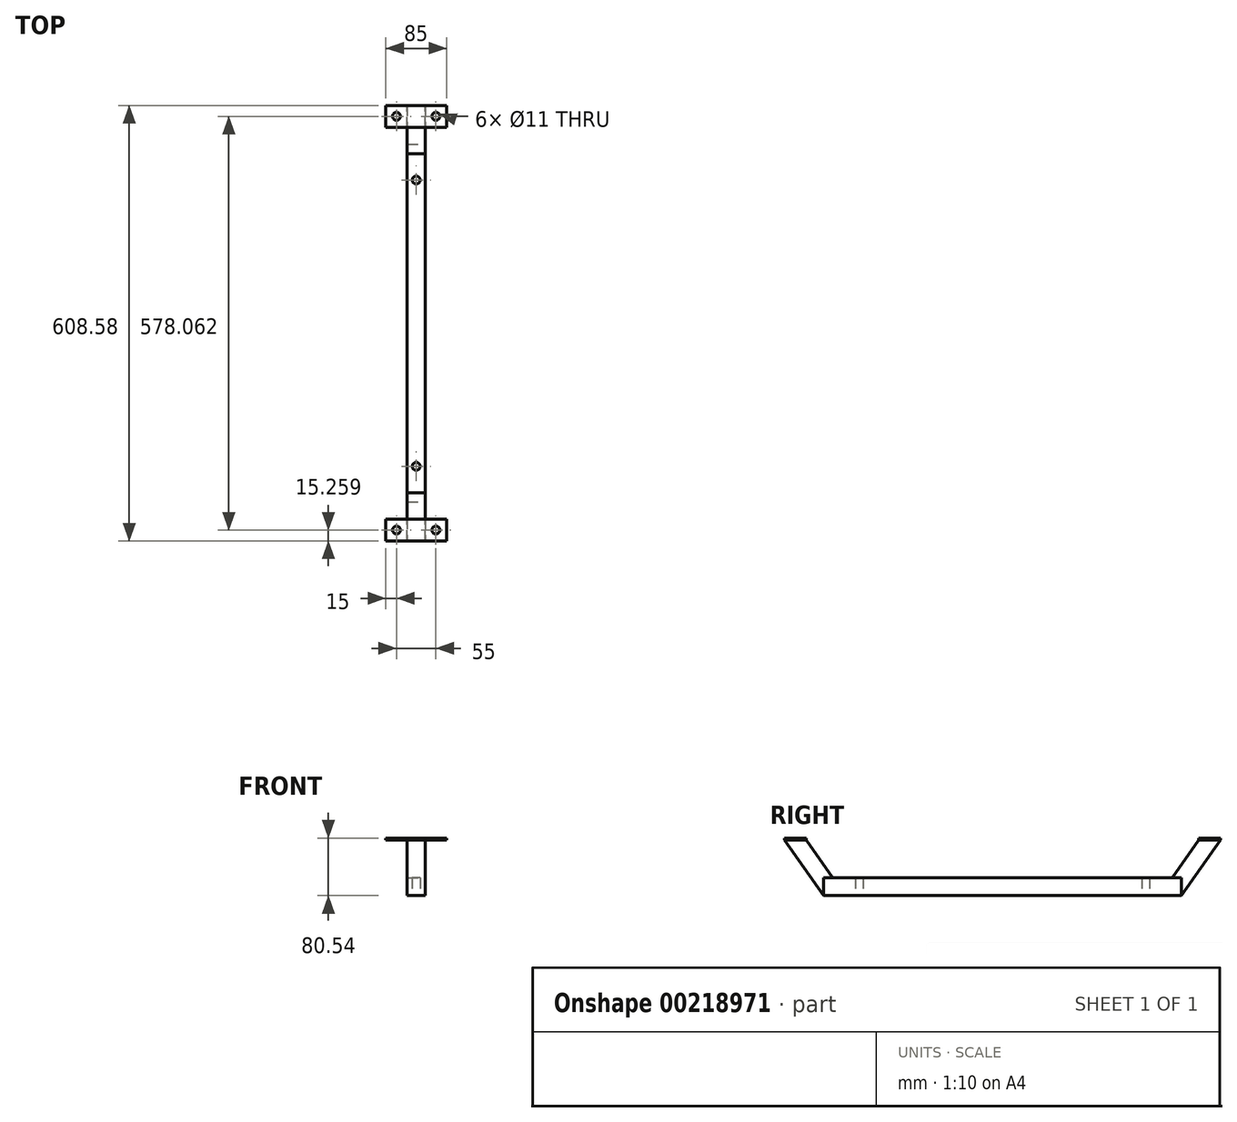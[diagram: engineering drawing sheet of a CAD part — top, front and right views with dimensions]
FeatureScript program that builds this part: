
annotation { "Feature Type Name" : "Feature", "Feature Type Description" : "" }
export const myFeature = defineFeature(function(context is Context, id is Id, definition is map)
    precondition{}
    {
        {
            var Q0;
            Q0=qCreatedBy(makeId("Top.planeOp"),FACE);
            var sketch = newSketch(context, id + "F0", { "sketchPlane" : qUnion([Q0])});
            skPoint(sketch, "E0", {"position": v(0, 200) * mm});
            skPoint(sketch, "E1.MirrorP", {"position": v(0, -200) * mm});
            skLineSegment(sketch, "E2", {"start": v(12.5, -250) * mm, "end": v(-12.5, -250) * mm});
            skLineSegment(sketch, "E3.MirrorCS", {"start": v(12.5, 250) * mm, "end": v(-12.5, 250) * mm});
            skLineSegment(sketch, "E4", {"start": v(-12.5, 250) * mm, "end": v(-12.5, -250) * mm});
            skLineSegment(sketch, "E5", {"start": v(12.5, -250) * mm, "end": v(12.5, 250) * mm});
            skCircle(sketch, "E6", {"center": v(0, 200) * mm, "radius": 5.5 * mm});
            skCircle(sketch, "E7", {"center": v(0, -200) * mm, "radius": 5.5 * mm});
            skSolve(sketch);
        }
        {
            var Q0;
            {var subQ2=sQuery(id+"F0.wireOp",EDGE,"E2");Q0=makeQuery(id+"F0.imprint","IMPRINT",FACE,{"disambiguationData":[TD([[makeQuery(id+"F0.imprint","IMPRINT",EDGE,{"derivedFrom":subQ2}),-1.0]])]});}
            extrude(context, id + "F1", {"entities" : qUnion([Q0]), "depth" : 25 * mm, "offsetDistance" : 25 * mm});
        }
        {
            var Q0;
            Q0=makeQuery(id+"F1.opExtrude","SWEPT_FACE",FACE,{"disambiguationData":[OSD([sQuery(id+"F0.wireOp",EDGE,"E5")])]});
            var sketch = newSketch(context, id + "F2", { "sketchPlane" : qUnion([Q0])});
            skLineSegment(sketch, "E8", {"start": v(-250, 0) * mm, "end": v(-304.3, 77.54) * mm});
            skLineSegment(sketch, "E9", {"start": v(-273.77, 77.54) * mm, "end": v(-236.99, 25) * mm});
            skLineSegment(sketch, "E10.MirrorCS", {"start": v(273.77, 77.54) * mm, "end": v(236.99, 25) * mm});
            skLineSegment(sketch, "E11.MirrorCS", {"start": v(250, 0) * mm, "end": v(304.3, 77.54) * mm});
            skLineSegment(sketch, "E12", {"start": v(-273.77, 77.54) * mm, "end": v(-294.25, 63.2) * mm});
            skLineSegment(sketch, "E13.MirrorCS", {"start": v(273.77, 77.54) * mm, "end": v(294.25, 63.2) * mm});
            skLineSegment(sketch, "E14", {"start": v(-304.3, 77.54) * mm, "end": v(-304.3, 82.54) * mm});
            skLineSegment(sketch, "E15", {"start": v(-273.77, 77.54) * mm, "end": v(-273.77, 82.54) * mm});
            skLineSegment(sketch, "E16", {"start": v(-304.3, 82.54) * mm, "end": v(-273.77, 82.54) * mm});
            skLineSegment(sketch, "E17", {"start": v(-304.3, 77.54) * mm, "end": v(-273.77, 77.54) * mm});
            skLineSegment(sketch, "E18.MirrorCS", {"start": v(304.3, 82.54) * mm, "end": v(273.77, 82.54) * mm});
            skLineSegment(sketch, "E19.MirrorCS", {"start": v(304.3, 77.54) * mm, "end": v(273.77, 77.54) * mm});
            skLineSegment(sketch, "E20.MirrorCS", {"start": v(273.77, 77.54) * mm, "end": v(273.77, 82.54) * mm});
            skLineSegment(sketch, "E21.MirrorCS", {"start": v(304.3, 77.54) * mm, "end": v(304.3, 82.54) * mm});
            skSolve(sketch);
        }
        {
            var Q0;
            Q0=makeQuery(id+"F2.imprint","IMPRINT",FACE,{"disambiguationData":[TD([[makeQuery(id+"F2.imprint","IMPRINT",EDGE,{"derivedFrom":sQuery(id+"F2.wireOp",EDGE,"E8")}),-1.0]])]});
            var Q1;
            {var subQ2=sQuery(id+"F2.wireOp",EDGE,"37a704e1-2d12-4eb0-b831-eae495b663a10.MirrorCS");Q1=makeQuery(id+"F2.imprint","IMPRINT",FACE,{"disambiguationData":[TD([[makeQuery(id+"F2.imprint","IMPRINT",EDGE,{"derivedFrom":subQ2}),1.0]])]});}
            var Q2;
            Q2=makeQuery(id+"F2.imprint","IMPRINT",FACE,{"disambiguationData":[TD([[makeQuery(id+"F2.imprint","IMPRINT",EDGE,{"derivedFrom":sQuery(id+"F2.wireOp",EDGE,"2267d19a-06c4-4bd6-b0c1-06ced329ed710.MirrorCS")}),1.0]])]});
            var Q3;
            Q3=makeQuery(id+"F2.imprint","IMPRINT",FACE,{"disambiguationData":[TD([[makeQuery(id+"F2.imprint","IMPRINT",EDGE,{"derivedFrom":sQuery(id+"F2.wireOp",EDGE,"TcwFsMnC-B8Dk-f2WK-MCm5-D9MKifv6v5wP")}),1.0]])]});
            var Q4;
            Q4=makeQuery(id+"F2.imprint","IMPRINT",FACE,{"disambiguationData":[TD([[makeQuery(id+"F2.imprint","IMPRINT",EDGE,{"derivedFrom":sQuery(id+"F2.wireOp",EDGE,"addbd2ca-d286-46d2-bc86-d6bb1087d67a0.MirrorCS")}),-1.0]])]});
            var Q5;
            {var subQ4=sQuery(id+"F2.wireOp",EDGE,"E10.MirrorCS");Q5=makeQuery(id+"F2.imprint","IMPRINT",FACE,{"disambiguationData":[TD([[makeQuery(id+"F2.imprint","IMPRINT",EDGE,{"derivedFrom":subQ4}),1.0]])]});}
            var Q6;
            {var subQ3=sQuery(id+"F2.wireOp",EDGE,"E9");Q6=makeQuery(id+"F2.imprint","IMPRINT",FACE,{"disambiguationData":[TD([[makeQuery(id+"F2.imprint","IMPRINT",EDGE,{"derivedFrom":subQ3}),-1.0]])]});}
            var Q7;
            {var subQ2=sQuery(id+"F2.wireOp",EDGE,"E13.MirrorCS");Q7=makeQuery(id+"F2.imprint","IMPRINT",FACE,{"disambiguationData":[TD([[makeQuery(id+"F2.imprint","IMPRINT",EDGE,{"derivedFrom":subQ2}),1.0]])]});}
            extrude(context, id + "F3", {"entities" : qUnion([Q0, Q1, Q2, Q3, Q4, Q5, Q6, Q7]), "oppositeDirection" : true, "depth" : 25 * mm, "offsetDistance" : 25 * mm});
        }
        {
            var Q0;
            Q0=makeQuery(id+"F3.opExtrude","SWEPT_FACE",FACE,{"disambiguationData":[OSD([sQuery(id+"F2.wireOp",EDGE,"E17")])]});
            var sketch = newSketch(context, id + "F4", { "sketchPlane" : qUnion([Q0])});
            skLineSegment(sketch, "E22", {"start": v(12.5, -273.77) * mm, "end": v(42.5, -273.77) * mm});
            skLineSegment(sketch, "E23", {"start": v(12.5, -304.3) * mm, "end": v(42.5, -304.3) * mm});
            skLineSegment(sketch, "E24", {"start": v(42.5, -304.3) * mm, "end": v(42.5, -273.77) * mm});
            skLineSegment(sketch, "E25", {"start": v(-12.5, -273.77) * mm, "end": v(-42.5, -273.77) * mm});
            skLineSegment(sketch, "E26", {"start": v(-12.5, -304.3) * mm, "end": v(-42.5, -304.3) * mm});
            skLineSegment(sketch, "E27", {"start": v(-42.5, -304.3) * mm, "end": v(-42.5, -273.77) * mm});
            skLineSegment(sketch, "E28.MirrorCS", {"start": v(42.5, 304.3) * mm, "end": v(42.5, 273.77) * mm});
            skLineSegment(sketch, "E29.MirrorCS", {"start": v(-42.5, 304.3) * mm, "end": v(-42.5, 273.77) * mm});
            skLineSegment(sketch, "E30", {"start": v(-42.5, 304.3) * mm, "end": v(42.5, 304.3) * mm});
            skLineSegment(sketch, "E31", {"start": v(42.5, 273.77) * mm, "end": v(-42.5, 273.77) * mm});
            skCircle(sketch, "E32", {"center": v(-27.5, -289.03) * mm, "radius": 5.5 * mm});
            skCircle(sketch, "E33", {"center": v(27.5, -289.03) * mm, "radius": 5.5 * mm});
            skCircle(sketch, "E34.MirrorC", {"center": v(27.5, 289.03) * mm, "radius": 5.5 * mm});
            skCircle(sketch, "E35.MirrorC", {"center": v(-27.5, 289.03) * mm, "radius": 5.5 * mm});
            skSolve(sketch);
        }
        {
            var Q0;
            Q0=makeQuery(id+"F4.imprint","IMPRINT",FACE,{"disambiguationData":[TD([[makeQuery(id+"F4.imprint","IMPRINT",EDGE,{"derivedFrom":sQuery(id+"F4.wireOp",EDGE,"E25")}),1.0]])]});
            var Q1;
            {var subQ0=sQuery(id+"F2.wireOp",EDGE,"E17");Q1=makeQuery(id+"F4.imprint","IMPRINT",FACE,{"disambiguationData":[TD([[makeQuery(id+"F4.imprint","IMPRINT",EDGE,{"derivedFrom":makeQuery(id+"F3.opExtrude","CAP_EDGE",EDGE,{"disambiguationData":[OSD([subQ0])],"isStart":true})}),1.0]])]});}
            var Q2;
            Q2=makeQuery(id+"F4.imprint","IMPRINT",FACE,{"disambiguationData":[TD([[makeQuery(id+"F4.imprint","IMPRINT",EDGE,{"derivedFrom":sQuery(id+"F4.wireOp",EDGE,"E22")}),-1.0]])]});
            var Q3;
            Q3=makeQuery(id+"F4.imprint","IMPRINT",FACE,{"disambiguationData":[TD([[makeQuery(id+"F4.imprint","IMPRINT",EDGE,{"derivedFrom":sQuery(id+"F4.wireOp",EDGE,"E28.MirrorCS")}),-1.0]])]});
            extrude(context, id + "F5", {"entities" : qUnion([Q0, Q1, Q2, Q3]), "operationType" : NewBodyOperationType.ADD, "depth" : 3 * mm, "offsetDistance" : 25 * mm});
        }
    });
